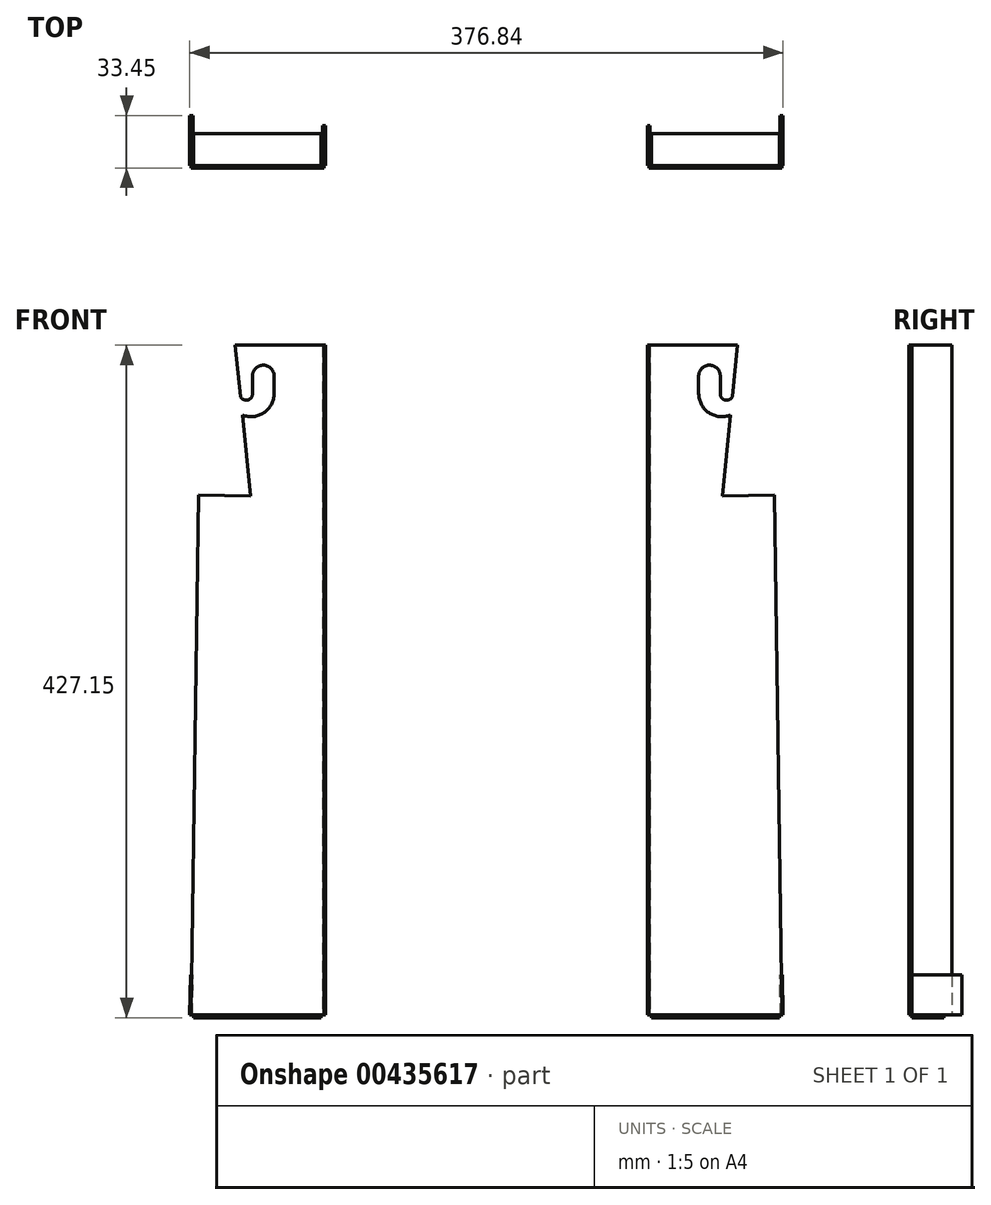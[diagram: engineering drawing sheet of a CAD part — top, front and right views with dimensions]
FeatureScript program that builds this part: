
annotation { "Feature Type Name" : "Feature", "Feature Type Description" : "" }
export const myFeature = defineFeature(function(context is Context, id is Id, definition is map)
    precondition{}
    {
        {
            var Q0;
            Q0=qCreatedBy(makeId("Front.planeOp"),FACE);
            var sketch = newSketch(context, id + "F0", { "sketchPlane" : qUnion([Q0])});
            skLineSegment(sketch, "E0", {"start": v(-159.5, 187.82) * mm, "end": v(-103.17, 187.82) * mm});
            skLineSegment(sketch, "E1", {"start": v(-103.17, 187.82) * mm, "end": v(-103.17, -237.63) * mm});
            skLineSegment(sketch, "E2", {"start": v(-103.17, -237.63) * mm, "end": v(-187.57, -237.63) * mm});
            skLineSegment(sketch, "E3", {"start": v(-187.57, -237.63) * mm, "end": v(-182.79, 92.54) * mm});
            skLineSegment(sketch, "E4", {"start": v(-182.79, 92.54) * mm, "end": v(-149.77, 92.06) * mm});
            skLineSegment(sketch, "E5", {"start": v(-159.5, 187.82) * mm, "end": v(-149.77, 92.06) * mm});
            skCircle(sketch, "E6", {"center": v(-141.69, 168.26) * mm, "radius": 6.86 * mm});
            skLineSegment(sketch, "E7.bottom", {"start": v(-148.54, 168.58) * mm, "end": v(-134.82, 168.58) * mm});
            skLineSegment(sketch, "E7.top", {"start": v(-148.54, 157.15) * mm, "end": v(-134.82, 157.15) * mm});
            skLineSegment(sketch, "E7.left", {"start": v(-148.54, 168.58) * mm, "end": v(-148.54, 157.15) * mm});
            skLineSegment(sketch, "E7.right", {"start": v(-134.82, 168.58) * mm, "end": v(-134.82, 157.15) * mm});
            skArc(sketch, "E8", {"start": v(-156.19, 155.19) * mm, "mid": v(-151.56, 153.03) * mm, "end": v(-148.54, 157.15) * mm});
            skArc(sketch, "E9", {"start": v(-155, 143.42) * mm, "mid": v(-141.28, 144.95) * mm, "end": v(-134.82, 157.15) * mm});
            skSolve(sketch);
        }
        {
            var Q0;
            {var subQ9=sQuery(id+"F0.wireOp",EDGE,"E0");Q0=makeQuery(id+"F0.imprint","IMPRINT",FACE,{"disambiguationData":[TD([[makeQuery(id+"F0.imprint","IMPRINT",EDGE,{"derivedFrom":subQ9}),-1.0]])]});}
            extrude(context, id + "F1", {"entities" : qUnion([Q0]), "depth" : 1.7 * mm, "offsetDistance" : 25.4 * mm});
        }
        {
            var Q0;
            Q0=makeQuery(id+"F1.opExtrude","SWEPT_FACE",FACE,{"disambiguationData":[OSD([sQuery(id+"F0.wireOp",EDGE,"E1")])]});
            var sketch = newSketch(context, id + "F2", { "sketchPlane" : qUnion([Q0])});
            skLineSegment(sketch, "E10.bottom", {"start": v(0, 187.82) * mm, "end": v(25.4, 187.82) * mm});
            skLineSegment(sketch, "E10.top", {"start": v(0, -237.63) * mm, "end": v(25.4, -237.63) * mm});
            skLineSegment(sketch, "E10.left", {"start": v(0, 187.82) * mm, "end": v(0, -237.63) * mm});
            skLineSegment(sketch, "E10.right", {"start": v(25.4, 187.82) * mm, "end": v(25.4, -237.63) * mm});
            skSolve(sketch);
        }
        {
            var Q0;
            Q0=makeQuery(id+"F2.imprint","IMPRINT",FACE,{"disambiguationData":[TD([[makeQuery(id+"F2.imprint","IMPRINT",EDGE,{"derivedFrom":sQuery(id+"F2.wireOp",EDGE,"E10.bottom")}),-1.0]])]});
            var Q1;
            Q1=makeQuery(id+"F1.opExtrude","SWEPT_FACE",FACE,{"disambiguationData":[OSD([sQuery(id+"F0.wireOp",EDGE,"E1")])]});
            extrude(context, id + "F3", {"entities" : qUnion([Q0]), "depth" : 1.7 * mm, "endBoundEntityFace" : qUnion([Q1]), "offsetDistance" : 25.4 * mm, "symmetric" : true});
        }
        {
            var Q0;
            Q0=makeQuery(id+"F1.opExtrude","SWEPT_FACE",FACE,{"disambiguationData":[OSD([sQuery(id+"F0.wireOp",EDGE,"E3")])]});
            var sketch = newSketch(context, id + "F4", { "sketchPlane" : qUnion([Q0])});
            skLineSegment(sketch, "E11.bottom", {"start": v(0, -240.32) * mm, "end": v(-31.75, -240.32) * mm});
            skLineSegment(sketch, "E11.top", {"start": v(0, -214.92) * mm, "end": v(-31.75, -214.92) * mm});
            skLineSegment(sketch, "E11.left", {"start": v(0, -240.32) * mm, "end": v(0, -214.92) * mm});
            skLineSegment(sketch, "E11.right", {"start": v(-31.75, -240.32) * mm, "end": v(-31.75, -214.92) * mm});
            skSolve(sketch);
        }
        {
            var Q0;
            Q0=makeQuery(id+"F4.imprint","IMPRINT",FACE,{"disambiguationData":[TD([[makeQuery(id+"F4.imprint","IMPRINT",EDGE,{"derivedFrom":sQuery(id+"F4.wireOp",EDGE,"E11.bottom")}),-1.0]])]});
            extrude(context, id + "F5", {"entities" : qUnion([Q0]), "depth" : 1.7 * mm, "offsetDistance" : 25.4 * mm, "symmetric" : true});
        }
        {
            var Q0;
            Q0=makeQuery(id+"F1.opExtrude","SWEPT_FACE",FACE,{"disambiguationData":[OSD([sQuery(id+"F0.wireOp",EDGE,"E2")])]});
            var sketch = newSketch(context, id + "F6", { "sketchPlane" : qUnion([Q0])});
            skLineSegment(sketch, "E12.bottom", {"start": v(-186.15, 0) * mm, "end": v(-104.87, 0) * mm});
            skLineSegment(sketch, "E12.top", {"start": v(-186.15, -20.32) * mm, "end": v(-104.87, -20.32) * mm});
            skLineSegment(sketch, "E12.left", {"start": v(-186.15, 0) * mm, "end": v(-186.15, -20.32) * mm});
            skLineSegment(sketch, "E12.right", {"start": v(-104.87, 0) * mm, "end": v(-104.87, -20.32) * mm});
            skSolve(sketch);
        }
        {
            var Q0;
            Q0=makeQuery(id+"F6.imprint","IMPRINT",FACE,{"disambiguationData":[TD([[makeQuery(id+"F6.imprint","IMPRINT",EDGE,{"derivedFrom":sQuery(id+"F6.wireOp",EDGE,"E12.bottom")}),1.0]])]});
            extrude(context, id + "F7", {"entities" : qUnion([Q0]), "depth" : 1.7 * mm, "offsetDistance" : 25.4 * mm});
        }
        {
            var Q0;
            Q0=makeQuery(id+"F1.opExtrude","SWEPT_BODY",BODY,{"disambiguationData":[OSD([sQuery(id+"F0.wireOp",EDGE,"E0"),sQuery(id+"F0.wireOp",EDGE,"E1"),sQuery(id+"F0.wireOp",EDGE,"E2"),sQuery(id+"F0.wireOp",EDGE,"E3"),sQuery(id+"F0.wireOp",EDGE,"E4"),sQuery(id+"F0.wireOp",EDGE,"E5"),sQuery(id+"F0.wireOp",EDGE,"E6"),sQuery(id+"F0.wireOp",EDGE,"E7.bottom"),sQuery(id+"F0.wireOp",EDGE,"E7.left"),sQuery(id+"F0.wireOp",EDGE,"E7.right"),sQuery(id+"F0.wireOp",EDGE,"E8"),sQuery(id+"F0.wireOp",EDGE,"E9")])]});
            var Q1;
            Q1=makeQuery(id+"F3.opExtrude","SWEPT_BODY",BODY,{"disambiguationData":[OSD([sQuery(id+"F2.wireOp",EDGE,"E10.bottom"),sQuery(id+"F2.wireOp",EDGE,"E10.top"),sQuery(id+"F2.wireOp",EDGE,"E10.left"),sQuery(id+"F2.wireOp",EDGE,"E10.right")])]});
            var Q2;
            Q2=makeQuery(id+"F5.opExtrude","SWEPT_BODY",BODY,{"disambiguationData":[OSD([sQuery(id+"F4.wireOp",EDGE,"E11.bottom"),sQuery(id+"F4.wireOp",EDGE,"E11.top"),sQuery(id+"F4.wireOp",EDGE,"E11.left"),sQuery(id+"F4.wireOp",EDGE,"E11.right")])]});
            var Q3;
            Q3=makeQuery(id+"F7.opExtrude","SWEPT_BODY",BODY,{"disambiguationData":[OSD([sQuery(id+"F6.wireOp",EDGE,"E12.bottom"),sQuery(id+"F6.wireOp",EDGE,"E12.top"),sQuery(id+"F6.wireOp",EDGE,"E12.left"),sQuery(id+"F6.wireOp",EDGE,"E12.right")])]});
            var Q4;
            Q4=qCreatedBy(makeId("Right.planeOp"),FACE);
            mirror(context, id + "F8", {"entities" : qUnion([Q0, Q1, Q2, Q3]), "mirrorPlane" : qUnion([Q4])});
        }
    });
